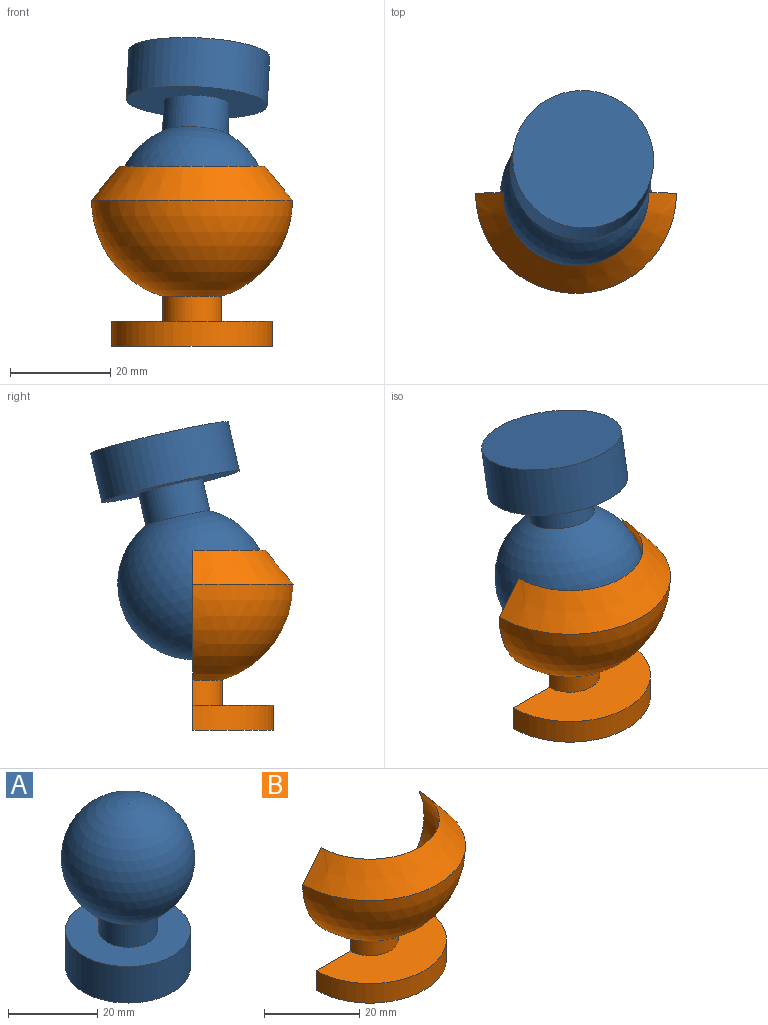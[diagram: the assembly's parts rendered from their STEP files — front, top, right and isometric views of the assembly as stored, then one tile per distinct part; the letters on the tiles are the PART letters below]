
ASSEMBLY  parts=2 mates=1
PART A: 5 faces, bbox 30x30x45 mm
  f0: plane 28.09x28.09mm, normal (0,0,-1), area 619.8mm2, adj f1
  f1: cylinder r=14.05mm len=28.09mm, axis (0,0,1), area 882.5mm2, adj f0,f2
  f2: plane 28.09x28.09mm, normal (0,0,1), area 485.2mm2, adj f1,f3
  f3: cylinder r=6.55mm len=13.09mm, axis (0,0,1), area 267.5mm2, adj f2,f4
  f4: sphere r=15mm, area 2685.7mm2, adj f3
PART B: 8 faces, bbox 40x20x35.9 mm
  f0: plane 32x16mm, normal (0,0,-1), area 402.1mm2, adj f1,f7
  f1: cylinder r=16mm len=32mm, axis (0,0,1), area 251.3mm2, adj f0,f2,f7
  f2: plane 32x16mm, normal (0,0,1), area 348mm2, adj f1,f3,f7
  f3: cylinder r=5.87mm len=11.74mm, axis (0,0,1), area 92.2mm2, adj f2,f4,f7
  f4: sphere r=20mm, area 1201.3mm2, adj f3,f5,f7
  f5: cone r=14.5mm half-angle=39.1deg, axis (0,0,-1), area 472.4mm2, adj f4,f6,f7
  f6: sphere r=16mm, area 1144.2mm2, adj f5,f7
  f7: plane 40x35.88mm, normal (0,1,0), area 461.5mm2, adj f0,f1,f2,f3,f4,f5,f6
PLACE A rot(axis=(1,0,-0.02),167.1deg) t=(-21.32,56.93,41.7)mm
PLACE B t=(-22.04,53.6,27.09)mm
MATE ball A.f1 <-> B.f7  axis (-0.05,-0.22,-0.97) through (-22.04,53.6,27.09)mm
